# Revit family: 2038593 Feilo Sylvania Lighting Fixture KOMETA 300 LED S 34 3K DALI
name_source: partatom
category: Lighting Fixtures
revit_build: Autodesk Revit 2017 (Build: 20190507_1515(x64)
units: mm (PartAtom-declared; Revit-internal decimal feet)

## family parameters
Cut with Voids When Loaded = No
Host = Face
Light Source = Yes
OmniClass Number = 23.80.70.00
OmniClass Title = Lighting
Part Type = Normal
Room Calculation Point = No
Round Connector Dimension = Use Diameter
Shared = No

## types (1)
- 2038593 KOMETA 300 LED S 34 3K DALI
    Apparent Load = 36 VA
    Assembly Code = D5020200
    AssetType = Fixed
    ClassificationName = Uniclass2015
    ClassificationValue = EF_70_80
    Color Filter = 16777215
    Cost = 0 $
    Default Elevation = 1219 mm
    Description = KOMETA 300 LED 3400LM 3000K DALI
    Dimming Lamp Color Temperature Shift = <None>
    DimmingControlOptions = Dimmable
    DocumentationLiterature = http://www.sylvania-lighting.com
    DurationUnit = hours
    ElectricShockClassification = Class II
    Emit Shape Visible in Rendering = No
    Emit from Circle Diameter = 610 mm
    ExpectedLife = 50000
    IfcExportAs = IfcLightFixtureType
    IfcExportType = IfcLightFixtureType
    ImpactProtectionIndex = IK02
    IngressProtection = IP20
    InputNominalFrequency = 50/60 Hz
    InputVoltage = 220-240V~
    Keynote = 16500
    Lamp = LED
    LampColourRenderingIndex = 80
    LampColourTemperature = 3000 K
    LampMacAdamStep = 3
    LampNominalLuminous = 3558 lm
    LampsType = LED
    LightOutputRatio = 100
    LuminousEfficacy = 99
    Manufacturer = Feilo Sylvania
    ManufacturerName = Feilo Sylvania
    Material = aluminium housing, polycarbonate diffuser
    Material_1_FEILO = <By Category>
    Material_2_FEILO = <By Category>
    Material_3_FEILO = <By Category>
    Material_4_FEILO = <By Category>
    Model = KOMETA 300 LED S 34 3K DALI
    ModelNumber = 2038593
    ModelReference = KOMETA 300 LED S 34 3K DALI
    Name = KOMETA 300 LED S 34 3K DALI
    NominalDepth = 300 mm
    NominalHeight = 110 mm
    NominalLength = 300 mm
    Photometric Web File = 2038593.ies
    PowerConsumption = 36
    PowerFactor = 0.98
    Tilt Angle = 90.00°
    Type Image = <None>
    TypeName = KOMETA 300 LED S 34 3K DALI
    URL = http://www.sylvania-lighting.com
    Voltage = 230 V
    Weight = 2.52 kg
    Width = 314 mm  [stored 1.03018 ft]

note: [stored X ft] marks values corroborated as IEEE doubles in the binary element streams (Revit-internal decimal feet)

## geometry (parser evidence)
native form markers: Sweep x3
no freeform markers — native parametric forms only
